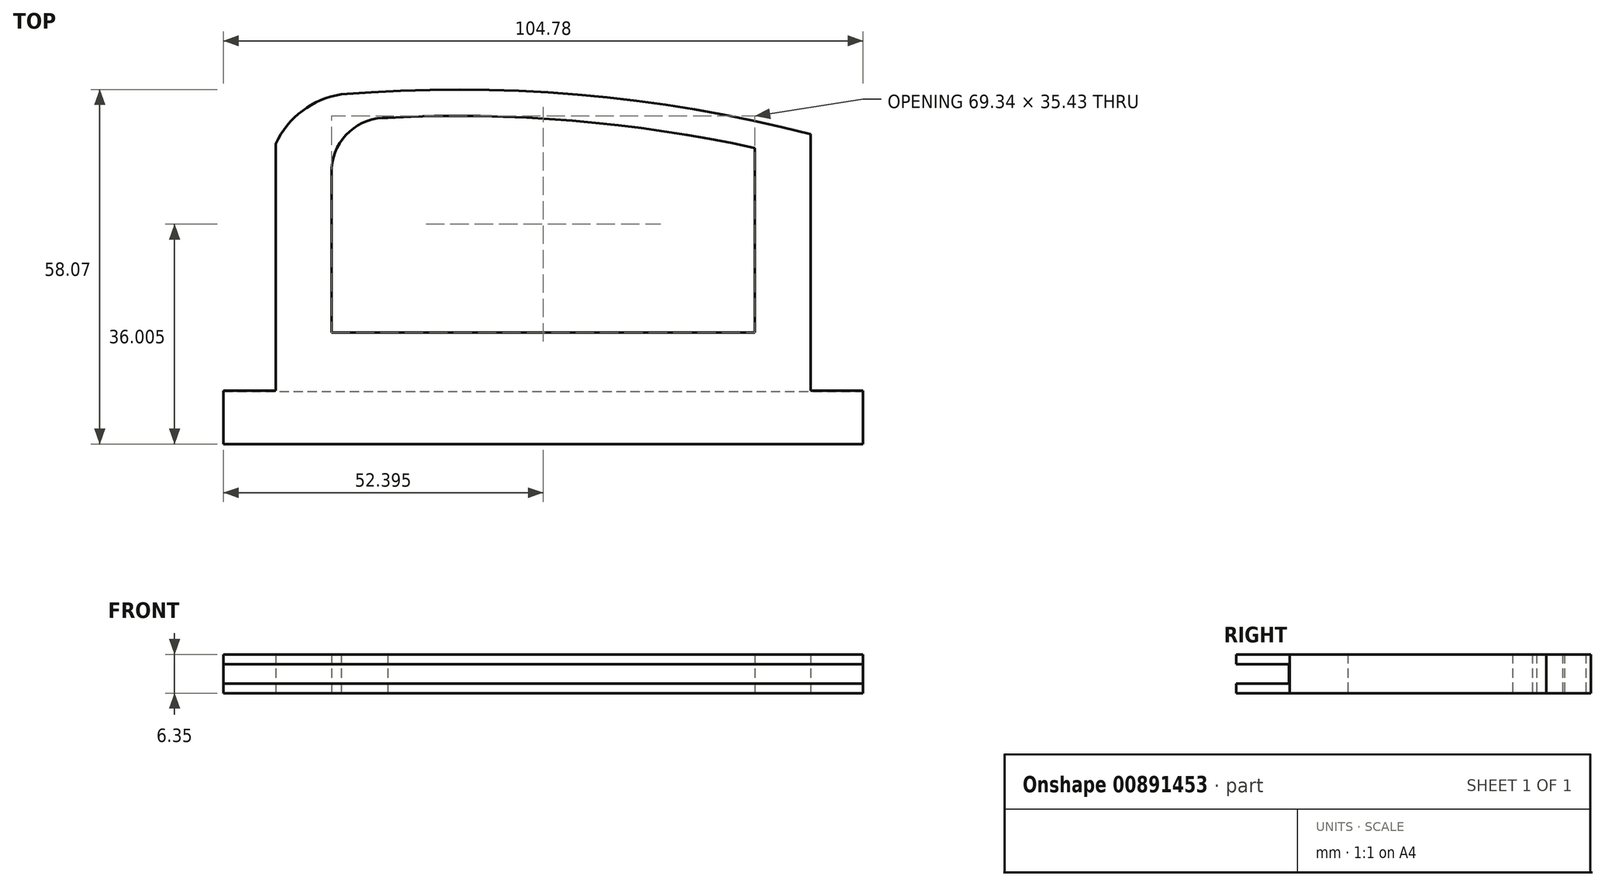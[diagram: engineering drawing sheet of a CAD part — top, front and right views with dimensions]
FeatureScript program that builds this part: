
annotation { "Feature Type Name" : "Feature", "Feature Type Description" : "" }
export const myFeature = defineFeature(function(context is Context, id is Id, definition is map)
    precondition{}
    {
        {
            var Q0;
            Q0=qCreatedBy(makeId("Top.planeOp"),FACE);
            var sketch = newSketch(context, id + "F0", { "sketchPlane" : qUnion([Q0])});
            skLineSegment(sketch, "E0.bottom", {"start": v(0, 0) * mm, "end": v(87.63, 0) * mm});
            skLineSegment(sketch, "E0.left", {"start": v(0, 8.76) * mm, "end": v(0, 49.17) * mm});
            skLineSegment(sketch, "E0.right", {"start": v(87.63, 8.76) * mm, "end": v(87.63, 50.77) * mm});
            skLineSegment(sketch, "E1.bottom", {"start": v(-8.58, 0) * mm, "end": v(96.2, 0) * mm});
            skLineSegment(sketch, "E1.top", {"start": v(-8.58, 8.76) * mm, "end": v(0, 8.76) * mm});
            skLineSegment(sketch, "E1.left", {"start": v(-8.58, 0) * mm, "end": v(-8.58, 8.76) * mm});
            skLineSegment(sketch, "E1.right", {"start": v(96.2, 0) * mm, "end": v(96.2, 8.76) * mm});
            skLineSegment(sketch, "E2.right", {"start": v(9.14, 18.29) * mm, "end": v(9.14, 45.24) * mm});
            skLineSegment(sketch, "E3.right", {"start": v(78.49, 18.29) * mm, "end": v(78.49, 48.5) * mm});
            skArc(sketch, "E4", {"start": v(87.63, 50.77) * mm, "mid": v(49.46, 57.24) * mm, "end": v(10.75, 57.29) * mm});
            skArc(sketch, "E5.0", {"start": v(9.3, 52.83) * mm, "mid": v(9.23, 52.83) * mm, "end": v(9.14, 52.83) * mm});
            skArc(sketch, "E5.1", {"start": v(78.49, 48.5) * mm, "mid": v(48.6, 52.98) * mm, "end": v(18.37, 53.47) * mm});
            skLineSegment(sketch, "E6.trimOffspring", {"start": v(87.63, 8.76) * mm, "end": v(96.2, 8.76) * mm});
            skArc(sketch, "E7", {"start": v(18.37, 53.47) * mm, "mid": v(12.1, 51.22) * mm, "end": v(9.14, 45.24) * mm});
            skArc(sketch, "E8", {"start": v(10.75, 57.29) * mm, "mid": v(4.34, 54.6) * mm, "end": v(0, 49.17) * mm});
            skLineSegment(sketch, "E9.top", {"start": v(9.14, 18.29) * mm, "end": v(78.49, 18.29) * mm});
            skLineSegment(sketch, "E9.left", {"start": v(0, 0) * mm, "end": v(0, 18.29) * mm});
            skLineSegment(sketch, "E9.right", {"start": v(87.63, 0) * mm, "end": v(87.63, 18.29) * mm});
            skSolve(sketch);
        }
        {
            var Q0;
            Q0=makeQuery(id+"F0.imprint","IMPRINT",FACE,{"disambiguationData":[TD([[makeQuery(id+"F0.imprint","IMPRINT",EDGE,{"derivedFrom":sQuery(id+"F0.wireOp",EDGE,"E1.top")}),-1.0]])]});
            var Q1;
            {var subQ1=sQuery(id+"F0.wireOp",EDGE,"E0.left");Q1=makeQuery(id+"F0.imprint","IMPRINT",FACE,{"disambiguationData":[TD([[makeQuery(id+"F0.imprint","IMPRINT",EDGE,{"derivedFrom":subQ1}),-1.0]])]});}
            var Q2;
            {var subQ0=sQuery(id+"F0.wireOp",EDGE,"E1.right");Q2=makeQuery(id+"F0.imprint","IMPRINT",FACE,{"disambiguationData":[TD([[makeQuery(id+"F0.imprint","IMPRINT",EDGE,{"derivedFrom":subQ0}),1.0]])]});}
            extrude(context, id + "F1", {"entities" : qUnion([Q0, Q1, Q2]), "depth" : 6.35 * mm, "offsetDistance" : 25.4 * mm});
        }
        {
            var Q0;
            Q0=makeQuery(id+"F1.opExtrude","SWEPT_FACE",FACE,{"disambiguationData":[OSD([sQuery(id+"F0.wireOp",EDGE,"E1.bottom")])]});
            var sketch = newSketch(context, id + "F2", { "sketchPlane" : qUnion([Q0])});
            skLineSegment(sketch, "E10.bottom", {"start": v(-8.58, 4.76) * mm, "end": v(96.2, 4.76) * mm});
            skLineSegment(sketch, "E10.top", {"start": v(-8.58, 1.59) * mm, "end": v(96.2, 1.59) * mm});
            skLineSegment(sketch, "E10.left", {"start": v(-8.58, 4.76) * mm, "end": v(-8.58, 1.59) * mm});
            skLineSegment(sketch, "E10.right", {"start": v(96.2, 4.76) * mm, "end": v(96.2, 1.59) * mm});
            skSolve(sketch);
        }
        {
            var Q0;
            Q0=makeQuery(id+"F2.imprint","IMPRINT",FACE,{"disambiguationData":[TD([[makeQuery(id+"F2.imprint","IMPRINT",EDGE,{"derivedFrom":sQuery(id+"F2.wireOp",EDGE,"E10.bottom")}),-1.0]])]});
            extrude(context, id + "F3", {"entities" : qUnion([Q0]), "operationType" : NewBodyOperationType.REMOVE, "oppositeDirection" : true, "depth" : 8.6 * mm, "offsetDistance" : 25.4 * mm});
        }
    });
